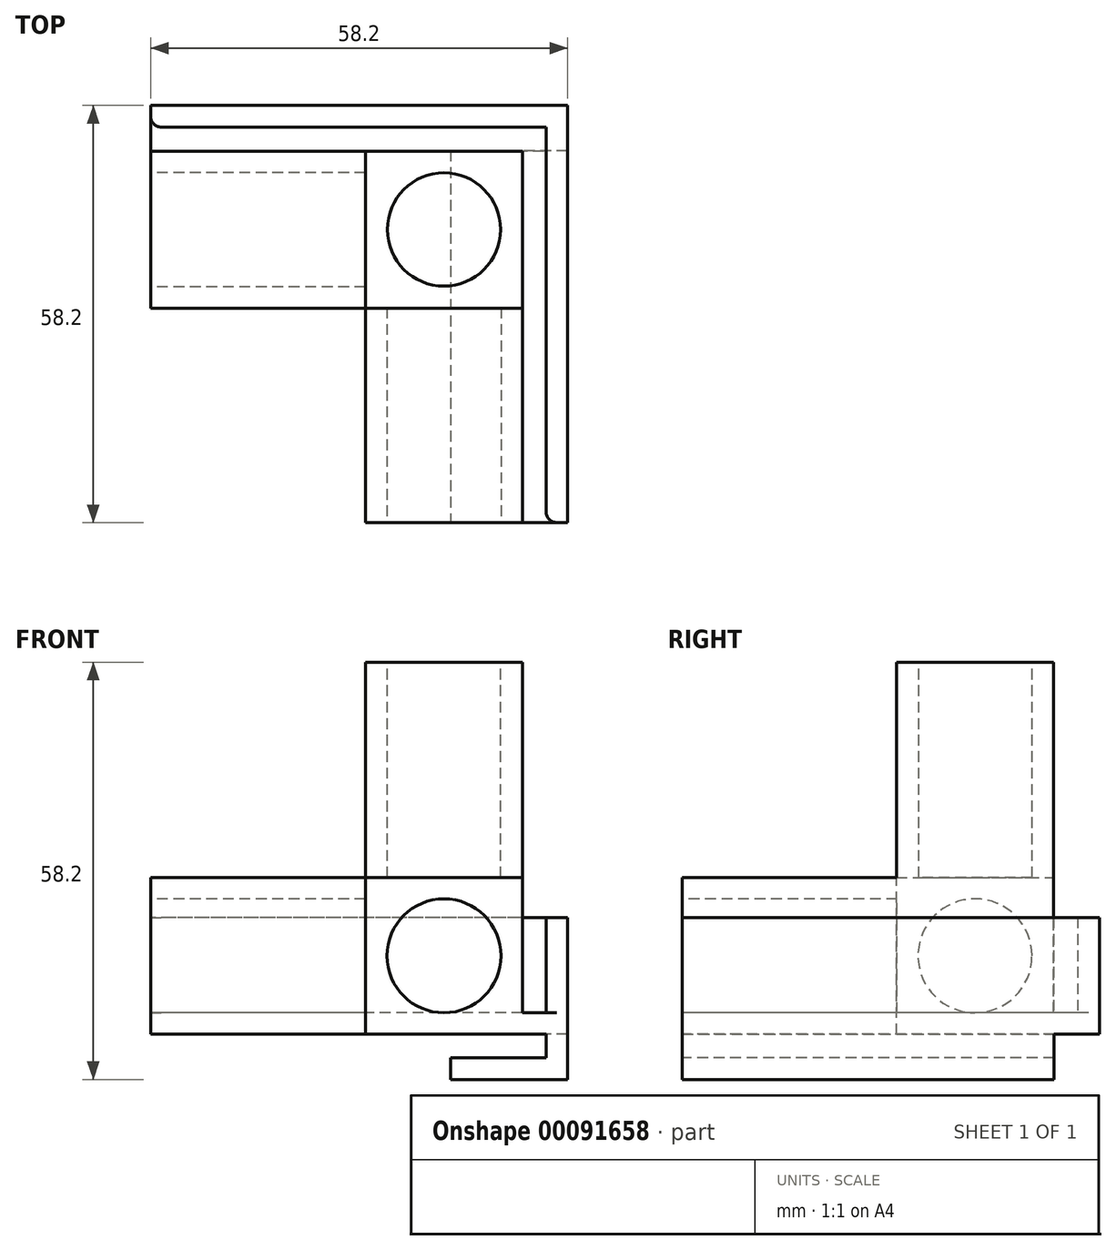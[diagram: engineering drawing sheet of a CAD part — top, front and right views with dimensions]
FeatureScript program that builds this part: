
annotation { "Feature Type Name" : "Feature", "Feature Type Description" : "" }
export const myFeature = defineFeature(function(context is Context, id is Id, definition is map)
    precondition{}
    {
        {
            var Q0;
            Q0=qCreatedBy(makeId("Front.planeOp"),FACE);
            var sketch = newSketch(context, id + "F0", { "sketchPlane" : qUnion([Q0])});
            skLineSegment(sketch, "E0.bottom", {"start": v(-42.3, 45.9) * mm, "end": v(-26.4, 45.9) * mm});
            skLineSegment(sketch, "E0.top", {"start": v(-42.3, 0) * mm, "end": v(-26.4, 0) * mm});
            skLineSegment(sketch, "E0.left", {"start": v(-42.3, 45.9) * mm, "end": v(-42.3, 0) * mm});
            skLineSegment(sketch, "E0.right", {"start": v(-26.4, 45.9) * mm, "end": v(-26.4, 15.9) * mm});
            skLineSegment(sketch, "E1.top", {"start": v(-42.3, 15.9) * mm, "end": v(-26.4, 15.9) * mm});
            skLineSegment(sketch, "E1.left", {"start": v(-42.3, 0) * mm, "end": v(-42.3, 15.9) * mm});
            skLineSegment(sketch, "E1.right", {"start": v(3.6, 0) * mm, "end": v(3.6, 15.9) * mm});
            skLineSegment(sketch, "E2", {"start": v(-26.4, 15.9) * mm, "end": v(-26.4, 0) * mm});
            skLineSegment(sketch, "E3", {"start": v(-26.4, 15.9) * mm, "end": v(3.6, 15.9) * mm});
            skLineSegment(sketch, "E4", {"start": v(-26.4, 0) * mm, "end": v(-26.4, 0) * mm});
            skLineSegment(sketch, "E5", {"start": v(-42.3, 15.9) * mm, "end": v(-42.3, 15.9) * mm});
            skLineSegment(sketch, "E6", {"start": v(-26.4, 0) * mm, "end": v(3.6, 0) * mm});
            skLineSegment(sketch, "E7.0", {"start": v(-45.3, 48.9) * mm, "end": v(-45.3, -3) * mm});
            skLineSegment(sketch, "E7.1", {"start": v(-45.3, -3) * mm, "end": v(-23.4, -3) * mm});
            skLineSegment(sketch, "E7.2", {"start": v(-23.4, 48.9) * mm, "end": v(-23.4, 18.9) * mm});
            skLineSegment(sketch, "E7.3", {"start": v(-23.4, 18.9) * mm, "end": v(6.6, 18.9) * mm});
            skLineSegment(sketch, "E7.4", {"start": v(6.6, -3) * mm, "end": v(6.6, 18.9) * mm});
            skLineSegment(sketch, "E7.5", {"start": v(-45.3, 48.9) * mm, "end": v(-23.4, 48.9) * mm});
            skLineSegment(sketch, "E7.6", {"start": v(-23.4, -3) * mm, "end": v(6.6, -3) * mm});
            skPoint(sketch, "E8", {"position": v(-34.36, 7.95) * mm});
            skPoint(sketch, "E8.positionSnap0", {"position": v(-26.4, 7.95) * mm});
            skPoint(sketch, "E8.positionSnap1", {"position": v(-34.36, 15.9) * mm});
            skCircle(sketch, "E9", {"center": v(-34.36, 7.95) * mm, "radius": 7.95 * mm});
            skLineSegment(sketch, "E10", {"start": v(-23.4, 18.9) * mm, "end": v(-45.3, 18.9) * mm});
            skLineSegment(sketch, "E11", {"start": v(-23.4, 18.9) * mm, "end": v(-23.4, -3) * mm});
            skSolve(sketch);
        }
        {
            var Q0;
            {var subQ1=sQuery(id+"F0.wireOp",EDGE,"E1.top");var subQ3=sQuery(id+"F0.wireOp",EDGE,"E9");var subQ4=makeQuery(id+"F0.imprint","INTERSECT",VERTEX,{"derivedFrom":[subQ1,subQ3]});Q0=makeQuery(id+"F0.imprint","IMPRINT",FACE,{"disambiguationData":[TD([[makeQuery(id+"F0.imprint","IMPRINT",EDGE,{"disambiguationData":[TD([[subQ4,-1.0]])],"derivedFrom":subQ3}),-1.0]])]});}
            var Q1;
            {var subQ0=sQuery(id+"F0.wireOp",EDGE,"E9");var subQ1=makeQuery(id+"F0.imprint","INTERSECT",VERTEX,{"derivedFrom":[sQuery(id+"F0.wireOp",EDGE,"E1.top"),subQ0]});Q1=makeQuery(id+"F0.imprint","IMPRINT",FACE,{"disambiguationData":[TD([[makeQuery(id+"F0.imprint","IMPRINT",EDGE,{"disambiguationData":[TD([[subQ1,1.0]])],"derivedFrom":subQ0}),1.0]])]});}
            var Q2;
            {var subQ5=sQuery(id+"F0.wireOp",EDGE,"E0.bottom");Q2=makeQuery(id+"F0.imprint","IMPRINT",FACE,{"disambiguationData":[TD([[makeQuery(id+"F0.imprint","IMPRINT",EDGE,{"derivedFrom":subQ5}),1.0]])]});}
            var Q3;
            {var subQ0=sQuery(id+"F0.wireOp",EDGE,"E1.right");Q3=makeQuery(id+"F0.imprint","IMPRINT",FACE,{"disambiguationData":[TD([[makeQuery(id+"F0.imprint","IMPRINT",EDGE,{"derivedFrom":subQ0}),1.0]])]});}
            var Q4;
            {var subQ0=sQuery(id+"F0.wireOp",EDGE,"E0.bottom");Q4=makeQuery(id+"F0.imprint","IMPRINT",FACE,{"disambiguationData":[TD([[makeQuery(id+"F0.imprint","IMPRINT",EDGE,{"derivedFrom":subQ0}),-1.0]])]});}
            var Q5;
            {var subQ0=sQuery(id+"F0.wireOp",EDGE,"E1.left");var subQ1=sQuery(id+"F0.wireOp",EDGE,"E0.top");var subQ2=makeQuery(id+"F0.imprint","INTERSECT",VERTEX,{"derivedFrom":[subQ1,subQ0]});Q5=makeQuery(id+"F0.imprint","IMPRINT",FACE,{"disambiguationData":[TD([[makeQuery(id+"F0.imprint","IMPRINT",EDGE,{"disambiguationData":[TD([[subQ2,-1.0]])],"derivedFrom":subQ1}),1.0]])]});}
            var Q6;
            {var subQ1=sQuery(id+"F0.wireOp",EDGE,"E0.top");var subQ3=sQuery(id+"F0.wireOp",EDGE,"E9");var subQ4=makeQuery(id+"F0.imprint","INTERSECT",VERTEX,{"derivedFrom":[subQ1,subQ3]});Q6=makeQuery(id+"F0.imprint","IMPRINT",FACE,{"disambiguationData":[TD([[makeQuery(id+"F0.imprint","IMPRINT",EDGE,{"disambiguationData":[TD([[subQ4,-1.0]])],"derivedFrom":subQ3}),-1.0]])]});}
            var Q7;
            {var subQ1=sQuery(id+"F0.wireOp",EDGE,"E1.top");var subQ3=sQuery(id+"F0.wireOp",EDGE,"E9");var subQ4=makeQuery(id+"F0.imprint","INTERSECT",VERTEX,{"derivedFrom":[subQ1,subQ3]});Q7=makeQuery(id+"F0.imprint","IMPRINT",FACE,{"disambiguationData":[TD([[makeQuery(id+"F0.imprint","IMPRINT",EDGE,{"disambiguationData":[TD([[subQ4,1.0]])],"derivedFrom":subQ3}),-1.0]])]});}
            var Q8;
            {var subQ5=sQuery(id+"F0.wireOp",EDGE,"E1.right");Q8=makeQuery(id+"F0.imprint","IMPRINT",FACE,{"disambiguationData":[TD([[makeQuery(id+"F0.imprint","IMPRINT",EDGE,{"derivedFrom":subQ5}),-1.0]])]});}
            var Q9;
            {var subQ4=sQuery(id+"F0.wireOp",EDGE,"E0.left");var subQ6=sQuery(id+"F0.wireOp",EDGE,"E10");var subQ8=makeQuery(id+"F0.imprint","INTERSECT",VERTEX,{"derivedFrom":[subQ4,subQ6]});Q9=makeQuery(id+"F0.imprint","IMPRINT",FACE,{"disambiguationData":[TD([[makeQuery(id+"F0.imprint","IMPRINT",EDGE,{"disambiguationData":[TD([[subQ8,1.0]])],"derivedFrom":subQ6}),1.0]])]});}
            var Q10;
            {var subQ3=sQuery(id+"F0.wireOp",EDGE,"E11");var subQ5=sQuery(id+"F0.wireOp",EDGE,"E3");var subQ8=makeQuery(id+"F0.imprint","INTERSECT",VERTEX,{"derivedFrom":[subQ5,subQ3]});Q10=makeQuery(id+"F0.imprint","IMPRINT",FACE,{"disambiguationData":[TD([[makeQuery(id+"F0.imprint","IMPRINT",EDGE,{"disambiguationData":[TD([[subQ8,-1.0]])],"derivedFrom":subQ3}),-1.0]])]});}
            var Q11;
            {var subQ14=sQuery(id+"F0.wireOp",EDGE,"E7.1");Q11=makeQuery(id+"F0.imprint","IMPRINT",FACE,{"disambiguationData":[TD([[makeQuery(id+"F0.imprint","IMPRINT",EDGE,{"derivedFrom":subQ14}),1.0]])]});}
            var Q12;
            {var subQ1=sQuery(id+"F0.wireOp",EDGE,"E0.right");var subQ3=sQuery(id+"F0.wireOp",EDGE,"E10");var subQ4=makeQuery(id+"F0.imprint","INTERSECT",VERTEX,{"derivedFrom":[subQ1,subQ3]});Q12=makeQuery(id+"F0.imprint","IMPRINT",FACE,{"disambiguationData":[TD([[makeQuery(id+"F0.imprint","IMPRINT",EDGE,{"disambiguationData":[TD([[subQ4,-1.0]])],"derivedFrom":subQ1}),1.0]])]});}
            extrude(context, id + "F1", {"entities" : qUnion([Q0, Q1, Q2, Q3, Q4, Q5, Q6, Q7, Q8, Q9, Q10, Q11, Q12]), "depth" : (15.9 + 6) * mm});
        }
        {
            var Q0;
            {var subQ14=sQuery(id+"F0.wireOp",EDGE,"E7.1");Q0=makeQuery(id+"F0.imprint","IMPRINT",FACE,{"disambiguationData":[TD([[makeQuery(id+"F0.imprint","IMPRINT",EDGE,{"derivedFrom":subQ14}),1.0]])]});}
            var Q1;
            {var subQ0=sQuery(id+"F0.wireOp",EDGE,"E9");var subQ1=makeQuery(id+"F0.imprint","INTERSECT",VERTEX,{"derivedFrom":[sQuery(id+"F0.wireOp",EDGE,"E1.top"),subQ0]});Q1=makeQuery(id+"F0.imprint","IMPRINT",FACE,{"disambiguationData":[TD([[makeQuery(id+"F0.imprint","IMPRINT",EDGE,{"disambiguationData":[TD([[subQ1,1.0]])],"derivedFrom":subQ0}),1.0]])]});}
            var Q2;
            {var subQ4=sQuery(id+"F0.wireOp",EDGE,"E0.left");var subQ6=sQuery(id+"F0.wireOp",EDGE,"E10");var subQ8=makeQuery(id+"F0.imprint","INTERSECT",VERTEX,{"derivedFrom":[subQ4,subQ6]});Q2=makeQuery(id+"F0.imprint","IMPRINT",FACE,{"disambiguationData":[TD([[makeQuery(id+"F0.imprint","IMPRINT",EDGE,{"disambiguationData":[TD([[subQ8,1.0]])],"derivedFrom":subQ6}),1.0]])]});}
            var Q3;
            {var subQ3=sQuery(id+"F0.wireOp",EDGE,"E11");var subQ5=sQuery(id+"F0.wireOp",EDGE,"E3");var subQ8=makeQuery(id+"F0.imprint","INTERSECT",VERTEX,{"derivedFrom":[subQ5,subQ3]});Q3=makeQuery(id+"F0.imprint","IMPRINT",FACE,{"disambiguationData":[TD([[makeQuery(id+"F0.imprint","IMPRINT",EDGE,{"disambiguationData":[TD([[subQ8,-1.0]])],"derivedFrom":subQ3}),-1.0]])]});}
            var Q4;
            {var subQ1=sQuery(id+"F0.wireOp",EDGE,"E0.right");var subQ3=sQuery(id+"F0.wireOp",EDGE,"E10");var subQ4=makeQuery(id+"F0.imprint","INTERSECT",VERTEX,{"derivedFrom":[subQ1,subQ3]});Q4=makeQuery(id+"F0.imprint","IMPRINT",FACE,{"disambiguationData":[TD([[makeQuery(id+"F0.imprint","IMPRINT",EDGE,{"disambiguationData":[TD([[subQ4,-1.0]])],"derivedFrom":subQ1}),1.0]])]});}
            var Q5;
            {var subQ1=sQuery(id+"F0.wireOp",EDGE,"E1.top");var subQ3=sQuery(id+"F0.wireOp",EDGE,"E9");var subQ4=makeQuery(id+"F0.imprint","INTERSECT",VERTEX,{"derivedFrom":[subQ1,subQ3]});Q5=makeQuery(id+"F0.imprint","IMPRINT",FACE,{"disambiguationData":[TD([[makeQuery(id+"F0.imprint","IMPRINT",EDGE,{"disambiguationData":[TD([[subQ4,1.0]])],"derivedFrom":subQ3}),-1.0]])]});}
            var Q6;
            {var subQ1=sQuery(id+"F0.wireOp",EDGE,"E1.top");var subQ3=sQuery(id+"F0.wireOp",EDGE,"E9");var subQ4=makeQuery(id+"F0.imprint","INTERSECT",VERTEX,{"derivedFrom":[subQ1,subQ3]});Q6=makeQuery(id+"F0.imprint","IMPRINT",FACE,{"disambiguationData":[TD([[makeQuery(id+"F0.imprint","IMPRINT",EDGE,{"disambiguationData":[TD([[subQ4,-1.0]])],"derivedFrom":subQ3}),-1.0]])]});}
            var Q7;
            {var subQ0=sQuery(id+"F0.wireOp",EDGE,"E1.left");var subQ1=sQuery(id+"F0.wireOp",EDGE,"E0.top");var subQ2=makeQuery(id+"F0.imprint","INTERSECT",VERTEX,{"derivedFrom":[subQ1,subQ0]});Q7=makeQuery(id+"F0.imprint","IMPRINT",FACE,{"disambiguationData":[TD([[makeQuery(id+"F0.imprint","IMPRINT",EDGE,{"disambiguationData":[TD([[subQ2,-1.0]])],"derivedFrom":subQ1}),1.0]])]});}
            var Q8;
            {var subQ1=sQuery(id+"F0.wireOp",EDGE,"E0.top");var subQ3=sQuery(id+"F0.wireOp",EDGE,"E9");var subQ4=makeQuery(id+"F0.imprint","INTERSECT",VERTEX,{"derivedFrom":[subQ1,subQ3]});Q8=makeQuery(id+"F0.imprint","IMPRINT",FACE,{"disambiguationData":[TD([[makeQuery(id+"F0.imprint","IMPRINT",EDGE,{"disambiguationData":[TD([[subQ4,-1.0]])],"derivedFrom":subQ3}),-1.0]])]});}
            extrude(context, id + "F2", {"entities" : qUnion([Q0, Q1, Q2, Q3, Q4, Q5, Q6, Q7, Q8]), "operationType" : NewBodyOperationType.ADD, "depth" : (15.8 + 6 + 30) * mm});
        }
        {
            var Q0;
            Q0=makeQuery(id+"F2.opExtrude","CAP_FACE",FACE,{"disambiguationData":[OSD([sQuery(id+"F0.wireOp",EDGE,"E7.0"),sQuery(id+"F0.wireOp",EDGE,"E7.1"),sQuery(id+"F0.wireOp",EDGE,"E10"),sQuery(id+"F0.wireOp",EDGE,"E11")])],"isStart":false});
            var sketch = newSketch(context, id + "F3", { "sketchPlane" : qUnion([Q0])});
            skCircle(sketch, "E12.0", {"center": v(-34.36, 7.95) * mm, "radius": 7.95 * mm});
            skSolve(sketch);
        }
        {
            var Q0;
            Q0=makeQuery(id+"F1.opExtrude","SWEPT_FACE",FACE,{"disambiguationData":[OSD([sQuery(id+"F0.wireOp",EDGE,"E7.5")])]});
            var sketch = newSketch(context, id + "F4", { "sketchPlane" : qUnion([Q0])});
            skPoint(sketch, "E13", {"position": v(-34.36, -3) * mm});
            skPoint(sketch, "E14", {"position": v(-26.4, -10.9) * mm});
            skPoint(sketch, "E15", {"position": v(-34.36, -10.9) * mm});
            skPoint(sketch, "E16", {"position": v(-62.98, 75) * mm});
            skPoint(sketch, "E17.orphan", {"position": v(-42.3, -3) * mm});
            skPoint(sketch, "E18.orphan", {"position": v(-26.4, -3) * mm});
            skPoint(sketch, "E19.orphan", {"position": v(-26.4, -18.8) * mm});
            skCircle(sketch, "E20", {"center": v(-34.36, -10.9) * mm, "radius": 7.9 * mm});
            skSolve(sketch);
        }
        {
            var Q0;
            Q0=makeQuery(id+"F1.opExtrude","SWEPT_FACE",FACE,{"disambiguationData":[OSD([sQuery(id+"F0.wireOp",EDGE,"E7.4")])]});
            var sketch = newSketch(context, id + "F5", { "sketchPlane" : qUnion([Q0])});
            skLineSegment(sketch, "E21.0", {"start": v(-18.9, 15.9) * mm, "end": v(-3, 15.9) * mm});
            skLineSegment(sketch, "E21.1", {"start": v(-18.9, 0) * mm, "end": v(-18.9, 15.9) * mm});
            skLineSegment(sketch, "E21.2", {"start": v(-18.9, 0) * mm, "end": v(-3, 0) * mm});
            skLineSegment(sketch, "E21.3", {"start": v(-3, 0) * mm, "end": v(-3, 15.9) * mm});
            skCircle(sketch, "E22", {"center": v(-10.95, 7.95) * mm, "radius": 7.95 * mm});
            skPoint(sketch, "E22.centerSnap0", {"position": v(-10.95, 0) * mm});
            skPoint(sketch, "E22.centerSnap1", {"position": v(-3, 7.95) * mm});
            skSolve(sketch);
        }
        {
            var Q0;
            Q0=makeQuery(id+"F3.imprint","IMPRINT",FACE,{"disambiguationData":[TD([[makeQuery(id+"F3.imprint","IMPRINT",EDGE,{"derivedFrom":sQuery(id+"F3.wireOp",EDGE,"E12.0")}),1.0]])]});
            extrude(context, id + "F6", {"entities" : qUnion([Q0]), "operationType" : NewBodyOperationType.REMOVE, "oppositeDirection" : true, "depth" : 30 * mm});
        }
        {
            var Q0;
            {var subQ0=sQuery(id+"F5.wireOp",EDGE,"E22");var subQ1=makeQuery(id+"F5.imprint","INTERSECT",VERTEX,{"derivedFrom":[sQuery(id+"F5.wireOp",EDGE,"E21.1"),subQ0]});Q0=makeQuery(id+"F5.imprint","IMPRINT",FACE,{"disambiguationData":[TD([[makeQuery(id+"F5.imprint","IMPRINT",EDGE,{"disambiguationData":[TD([[subQ1,1.0]])],"derivedFrom":subQ0}),1.0]])]});}
            extrude(context, id + "F7", {"entities" : qUnion([Q0]), "operationType" : NewBodyOperationType.REMOVE, "oppositeDirection" : true, "depth" : 30 * mm});
        }
        {
            var Q0;
            Q0=makeQuery(id+"F4.imprint","IMPRINT",FACE,{"disambiguationData":[TD([[makeQuery(id+"F4.imprint","IMPRINT",EDGE,{"derivedFrom":sQuery(id+"F4.wireOp",EDGE,"E20")}),1.0]])]});
            var Q1;
            Q1=sQuery(id+"F4.wireOp",EDGE,"E20");
            extrude(context, id + "F8", {"entities" : qUnion([Q0]), "operationType" : NewBodyOperationType.REMOVE, "surfaceEntities" : qUnion([Q1]), "oppositeDirection" : true, "depth" : 30 * mm});
        }
        {
            var Q0;
            Q0=makeQuery(id+"F2.opExtrude","CAP_FACE",FACE,{"disambiguationData":[OSD([sQuery(id+"F0.wireOp",EDGE,"E7.0"),sQuery(id+"F0.wireOp",EDGE,"E7.1"),sQuery(id+"F0.wireOp",EDGE,"E10"),sQuery(id+"F0.wireOp",EDGE,"E11")])],"isStart":false});
            var sketch = newSketch(context, id + "F9", { "sketchPlane" : qUnion([Q0])});
            skLineSegment(sketch, "E23", {"start": v(-45.3, -3) * mm, "end": v(-51.6, -3) * mm});
            skLineSegment(sketch, "E24", {"start": v(-51.6, -3) * mm, "end": v(-51.6, 13.3) * mm});
            skLineSegment(sketch, "E25", {"start": v(-51.6, 13.3) * mm, "end": v(-48.6, 13.3) * mm});
            skLineSegment(sketch, "E26", {"start": v(-48.6, 13.3) * mm, "end": v(-48.6, 0) * mm});
            skLineSegment(sketch, "E27", {"start": v(-48.6, 0) * mm, "end": v(-45.3, 0) * mm});
            skSolve(sketch);
        }
        {
            var Q0;
            {var subQ0=sQuery(id+"F9.wireOp",EDGE,"E23");Q0=makeQuery(id+"F9.imprint","IMPRINT",FACE,{"disambiguationData":[TD([[makeQuery(id+"F9.imprint","IMPRINT",EDGE,{"derivedFrom":subQ0}),-1.0]])]});}
            extrude(context, id + "F10", {"entities" : qUnion([Q0]), "operationType" : NewBodyOperationType.ADD, "oppositeDirection" : true, "depth" : (6 + 15.9 + 30 + 6.3) * mm});
        }
        {
            var Q0;
            Q0=makeQuery(id+"F1.opExtrude","SWEPT_FACE",FACE,{"disambiguationData":[OSD([sQuery(id+"F0.wireOp",EDGE,"E7.4")])]});
            var sketch = newSketch(context, id + "F11", { "sketchPlane" : qUnion([Q0])});
            skLineSegment(sketch, "E28.0.0", {"start": v(6.4, 0) * mm, "end": v(0, 0) * mm});
            skLineSegment(sketch, "E28.0.1", {"start": v(0, 0) * mm, "end": v(0, -3) * mm});
            skLineSegment(sketch, "E28.0.2", {"start": v(0, -3) * mm, "end": v(6.4, -3) * mm});
            skLineSegment(sketch, "E28.0.3", {"start": v(6.4, -3) * mm, "end": v(6.4, 0) * mm});
            skLineSegment(sketch, "E29.0", {"start": v(6.4, 13.3) * mm, "end": v(6.4, 0) * mm});
            skLineSegment(sketch, "E30", {"start": v(6.4, 13.3) * mm, "end": v(3.4, 13.3) * mm});
            skLineSegment(sketch, "E31", {"start": v(3.4, 13.3) * mm, "end": v(3.4, 0) * mm});
            skSolve(sketch);
        }
        {
            var Q0;
            Q0=qSketchRegion(id+"F11",true);
            extrude(context, id + "F12", {"entities" : qUnion([Q0]), "operationType" : NewBodyOperationType.ADD, "endBound" : BoundingType.UP_TO_NEXT, "oppositeDirection" : true, "depth" : 25 * mm});
        }
        {
            var Q0;
            Q0=makeQuery(id+"F12.opExtrude","CAP_EDGE",EDGE,{"disambiguationData":[OSD([sQuery(id+"F11.wireOp",EDGE,"E31")])],"isStart":true});
            var Q1;
            Q1=makeQuery(id+"F10.opExtrude","CAP_EDGE",EDGE,{"disambiguationData":[OSD([sQuery(id+"F9.wireOp",EDGE,"E26")])],"isStart":true});
            fillet(context, id + "F13", {"entities" : qUnion([Q0, Q1]), "radius" : 1.5 * mm, "tangentPropagation" : true, "allowEdgeOverflow" : false});
        }
        {
            var Q0;
            Q0=makeQuery(id+"F1.opExtrude","SWEPT_BODY",BODY,{"disambiguationData":[OSD([sQuery(id+"F0.wireOp",EDGE,"E7.0"),sQuery(id+"F0.wireOp",EDGE,"E7.1"),sQuery(id+"F0.wireOp",EDGE,"E7.2"),sQuery(id+"F0.wireOp",EDGE,"E7.3"),sQuery(id+"F0.wireOp",EDGE,"E7.4"),sQuery(id+"F0.wireOp",EDGE,"E7.5"),sQuery(id+"F0.wireOp",EDGE,"E7.6")])]});
            var Q1;
            Q1=makeQuery(id+"F12.boolean.opBoolean","MERGE",FACE,{"derivedFrom":[makeQuery(id+"F1.opExtrude","SWEPT_FACE",FACE,{"disambiguationData":[OSD([sQuery(id+"F0.wireOp",EDGE,"E7.4")])]}),makeQuery(id+"F12.opExtrude","CAP_FACE",FACE,{"disambiguationData":[OSD([sQuery(id+"F11.wireOp",EDGE,"E28.0.0"),sQuery(id+"F11.wireOp",EDGE,"E28.0.1"),sQuery(id+"F11.wireOp",EDGE,"E28.0.2"),sQuery(id+"F11.wireOp",EDGE,"E28.0.3"),sQuery(id+"F11.wireOp",EDGE,"E29.0"),sQuery(id+"F11.wireOp",EDGE,"E30"),sQuery(id+"F11.wireOp",EDGE,"E31")])],"isStart":true})]});
            mirror(context, id + "F14", {"entities" : qUnion([Q0]), "mirrorPlane" : qUnion([Q1])});
        }
        {
            var Q0;
            Q0=makeQuery(id+"F1.opExtrude","SWEPT_BODY",BODY,{"disambiguationData":[OSD([sQuery(id+"F0.wireOp",EDGE,"E7.0"),sQuery(id+"F0.wireOp",EDGE,"E7.1"),sQuery(id+"F0.wireOp",EDGE,"E7.2"),sQuery(id+"F0.wireOp",EDGE,"E7.3"),sQuery(id+"F0.wireOp",EDGE,"E7.4"),sQuery(id+"F0.wireOp",EDGE,"E7.5"),sQuery(id+"F0.wireOp",EDGE,"E7.6")])]});
            deleteBodies(context, id + "F15", {"entities" : qUnion([Q0])});
        }
        {
            var Q0;
            {var subQ0=sQuery(id+"F0.wireOp",EDGE,"E7.0");Q0=makeQuery(id+"F14.opPattern","COPY",FACE,{"derivedFrom":makeQuery(id+"F10.boolean.opBoolean","MERGE",FACE,{"derivedFrom":[makeQuery(id+"F2.opExtrude","CAP_FACE",FACE,{"disambiguationData":[OSD([subQ0,sQuery(id+"F0.wireOp",EDGE,"E7.1"),sQuery(id+"F0.wireOp",EDGE,"E10"),sQuery(id+"F0.wireOp",EDGE,"E11")])],"isStart":false}),makeQuery(id+"F10.opExtrude","CAP_FACE",FACE,{"disambiguationData":[OSD([subQ0,sQuery(id+"F9.wireOp",EDGE,"E23"),sQuery(id+"F9.wireOp",EDGE,"E24"),sQuery(id+"F9.wireOp",EDGE,"E25"),sQuery(id+"F9.wireOp",EDGE,"E26"),sQuery(id+"F9.wireOp",EDGE,"E27")])],"isStart":true})]}),"instanceName":"1"});}
            var sketch = newSketch(context, id + "F16", { "sketchPlane" : qUnion([Q0])});
            skLineSegment(sketch, "E32", {"start": v(64.8, -3) * mm, "end": v(64.8, -9.3) * mm});
            skLineSegment(sketch, "E33", {"start": v(64.8, -9.3) * mm, "end": v(48.5, -9.3) * mm});
            skLineSegment(sketch, "E34", {"start": v(48.5, -9.3) * mm, "end": v(48.5, -6.3) * mm});
            skLineSegment(sketch, "E35", {"start": v(48.5, -6.3) * mm, "end": v(61.8, -6.3) * mm});
            skLineSegment(sketch, "E36", {"start": v(61.8, -6.3) * mm, "end": v(61.8, -3) * mm});
            skSolve(sketch);
        }
        {
            var Q0;
            {var subQ0=sQuery(id+"F16.wireOp",EDGE,"E32");Q0=makeQuery(id+"F16.imprint","IMPRINT",FACE,{"disambiguationData":[TD([[makeQuery(id+"F16.imprint","IMPRINT",EDGE,{"derivedFrom":subQ0}),-1.0]])]});}
            extrude(context, id + "F17", {"entities" : qUnion([Q0]), "operationType" : NewBodyOperationType.ADD, "oppositeDirection" : true, "depth" : (6 + 15.9 + 30) * mm});
        }
    });
